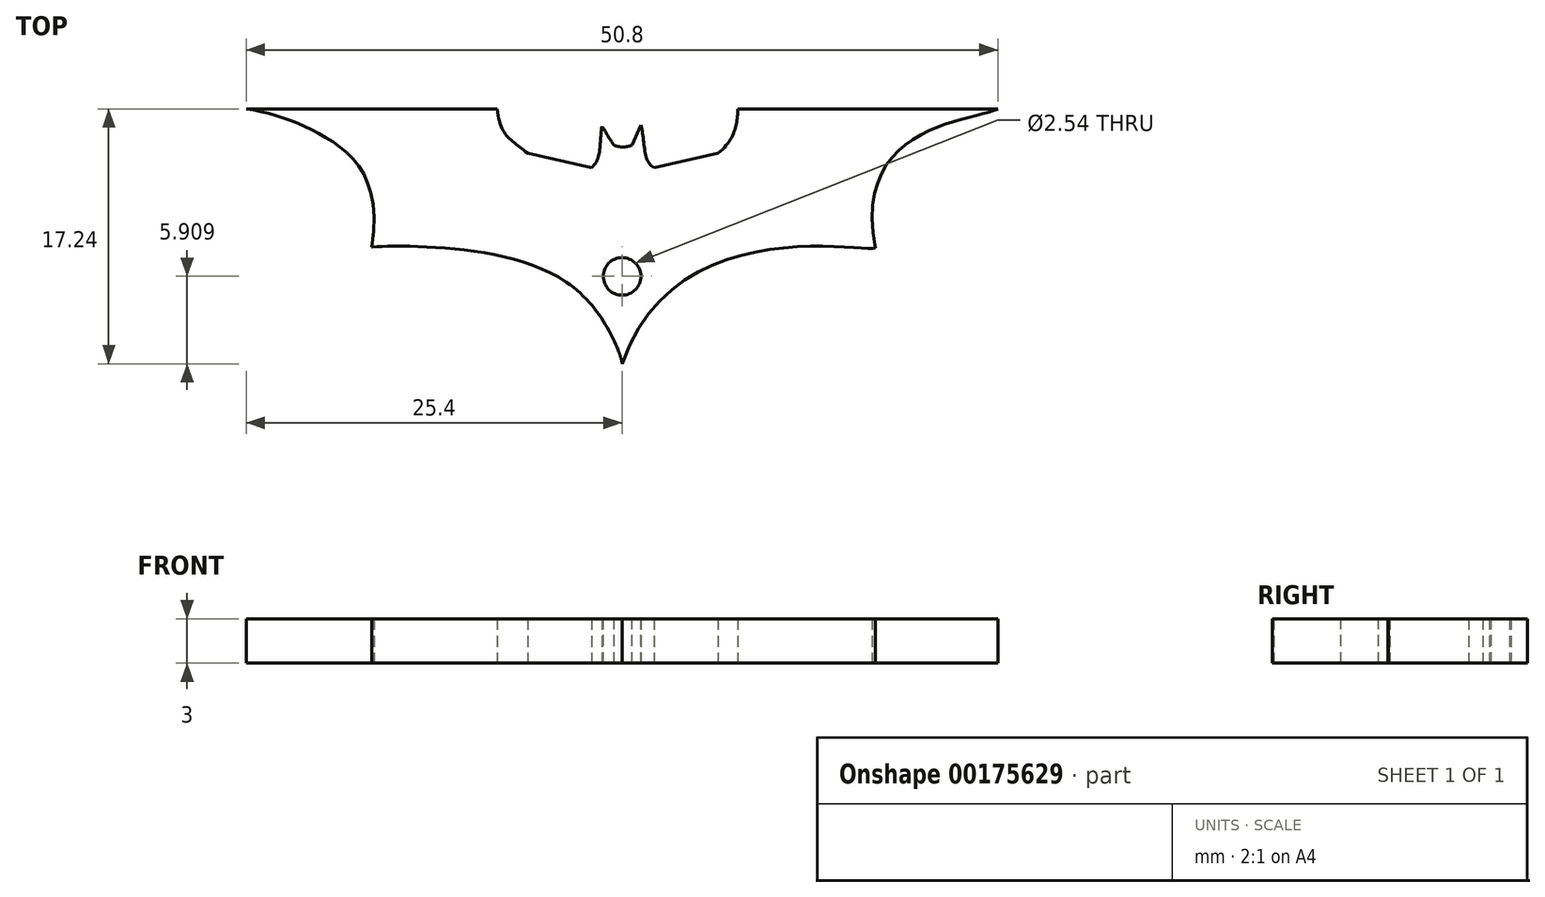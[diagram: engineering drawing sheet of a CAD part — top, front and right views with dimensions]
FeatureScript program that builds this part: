
annotation { "Feature Type Name" : "Feature", "Feature Type Description" : "" }
export const myFeature = defineFeature(function(context is Context, id is Id, definition is map)
    precondition{}
    {
        {
            var Q0;
            Q0=qCreatedBy(makeId("Top.planeOp"),FACE);
            var sketch = newSketch(context, id + "F0", { "sketchPlane" : qUnion([Q0])});
            skLineSegment(sketch, "E0", {"start": v(-25.4, 7.55) * mm, "end": v(-8.43, 7.55) * mm});
            skLineSegment(sketch, "E1", {"start": v(7.83, 7.55) * mm, "end": v(25.4, 7.55) * mm});
            skLineSegment(sketch, "E2", {"start": v(-6.39, 4.53) * mm, "end": v(-2.06, 3.58) * mm});
            skLineSegment(sketch, "E3", {"start": v(2.17, 3.58) * mm, "end": v(6.5, 4.53) * mm});
            skFitSpline(sketch, "E4", {"points": [v(-25.4, 7.55) * mm, v(-20.42, 5.83) * mm, v(-16.9, -1.79) * mm], "startDerivative": vector(11.89, -1.77) * mm, "endDerivative": vector(-4.02, -25.55) * mm});
            skFitSpline(sketch, "E5", {"points": [v(-16.9, -1.79) * mm, v(-3.77, -4.17) * mm, v(0, -9.61) * mm, v(0, -9.71) * mm], "startDerivative": vector(11.09, 0.53) * mm, "endDerivative": vector(-0.62, -1.23) * mm});
            skFitSpline(sketch, "E6", {"points": [v(0.01, -9.7) * mm, v(17.12, -1.86) * mm], "startDerivative": vector(10.4, 30.75) * mm, "endDerivative": vector(3.02, 0.9) * mm});
            skFitSpline(sketch, "E7", {"points": [v(17.12, -1.86) * mm, v(25.4, 7.55) * mm], "startDerivative": vector(-4.83, 25.07) * mm, "endDerivative": vector(5.9, 2.68) * mm});
            skFitSpline(sketch, "E8", {"points": [v(6.5, 4.53) * mm, v(7.83, 7.55) * mm], "startDerivative": vector(3.62, 3.17) * mm, "endDerivative": vector(0.15, 2.98) * mm});
            skFitSpline(sketch, "E9", {"points": [v(-6.39, 4.53) * mm, v(-8.43, 7.55) * mm], "startDerivative": vector(-3.17, 2.72) * mm, "endDerivative": vector(-0.45, 5.55) * mm});
            skFitSpline(sketch, "E10", {"points": [v(-2.06, 3.58) * mm, v(-1.35, 6.35) * mm], "startDerivative": vector(2.27, 1.81) * mm, "endDerivative": vector(0.6, 2.67) * mm});
            skFitSpline(sketch, "E11", {"points": [v(-1.35, 6.35) * mm, v(-0.55, 5.09) * mm], "startDerivative": vector(0.9, -1.16) * mm, "endDerivative": vector(0.9, -1.16) * mm});
            skFitSpline(sketch, "E12", {"points": [v(1.26, 6.45) * mm, v(2.17, 3.58) * mm], "startDerivative": vector(0.9, -2.9) * mm, "endDerivative": vector(2.42, -0.9) * mm});
            skFitSpline(sketch, "E13", {"points": [v(-0.55, 5.09) * mm, v(0.66, 5.09) * mm], "startDerivative": vector(1.15, -0.5) * mm, "endDerivative": vector(1.1, 0.5) * mm});
            skLineSegment(sketch, "E14", {"start": v(1.26, 6.45) * mm, "end": v(0.66, 5.09) * mm});
            skFitSpline(sketch, "E15", {"points": [v(-25.4, 7.55) * mm, v(-20.42, 5.83) * mm, v(-16.9, -1.79) * mm], "startDerivative": vector(11.89, -1.77) * mm, "endDerivative": vector(-4.02, -25.55) * mm});
            skFitSpline(sketch, "E16", {"points": [v(-16.9, -1.79) * mm, v(-3.77, -4.17) * mm, v(0.01, -9.7) * mm], "startDerivative": vector(10.58, 0.5) * mm, "endDerivative": vector(0.07, -2.6) * mm});
            skLineSegment(sketch, "E17", {"start": v(-25.4, 7.55) * mm, "end": v(25.4, 7.55) * mm});
            skPoint(sketch, "E18", {"position": v(0, 7.55) * mm});
            skSolve(sketch);
        }
        {
            var Q0;
            {var subQ0=sQuery(id+"F0.wireOp",EDGE,"E16");var subQ1=sQuery(id+"F0.wireOp",EDGE,"E5");var subQ3=makeQuery(id+"F0.imprint","INTERSECT",VERTEX,{"disambiguationData":[OD(1.0)],"derivedFrom":[subQ1,subQ0]});Q0=makeQuery(id+"F0.imprint","IMPRINT",FACE,{"disambiguationData":[TD([[makeQuery(id+"F0.imprint","IMPRINT",EDGE,{"disambiguationData":[TD([[subQ3,1.0]])],"derivedFrom":subQ1}),1.0]])]});}
            var Q1;
            {var subQ0=sQuery(id+"F0.wireOp",EDGE,"E16");var subQ1=sQuery(id+"F0.wireOp",EDGE,"E5");var subQ2=makeQuery(id+"F0.imprint","INTERSECT",VERTEX,{"disambiguationData":[OD(1.0)],"derivedFrom":[subQ1,subQ0]});Q1=makeQuery(id+"F0.imprint","IMPRINT",FACE,{"disambiguationData":[TD([[makeQuery(id+"F0.imprint","IMPRINT",EDGE,{"disambiguationData":[TD([[subQ2,-1.0]])],"derivedFrom":subQ1}),-1.0]])]});}
            var Q2;
            {var subQ0=sQuery(id+"F0.wireOp",EDGE,"E16");var subQ1=sQuery(id+"F0.wireOp",EDGE,"E5");var subQ2=makeQuery(id+"F0.imprint","INTERSECT",VERTEX,{"disambiguationData":[OD(2.0)],"derivedFrom":[subQ1,subQ0]});Q2=makeQuery(id+"F0.imprint","IMPRINT",FACE,{"disambiguationData":[TD([[makeQuery(id+"F0.imprint","IMPRINT",EDGE,{"disambiguationData":[TD([[subQ2,-1.0]])],"derivedFrom":subQ1}),1.0]])]});}
            var Q3;
            {var subQ0=sQuery(id+"F0.wireOp",EDGE,"E16");var subQ1=sQuery(id+"F0.wireOp",EDGE,"E5");var subQ2=makeQuery(id+"F0.imprint","INTERSECT",VERTEX,{"disambiguationData":[OD(0.0)],"derivedFrom":[subQ1,subQ0]});Q3=makeQuery(id+"F0.imprint","IMPRINT",FACE,{"disambiguationData":[TD([[makeQuery(id+"F0.imprint","IMPRINT",EDGE,{"disambiguationData":[TD([[subQ2,1.0]])],"derivedFrom":subQ1}),-1.0]])]});}
            var Q4;
            Q4=makeQuery(id+"F0.imprint","IMPRINT",FACE,{"disambiguationData":[TD([[makeQuery(id+"F0.imprint","IMPRINT",EDGE,{"derivedFrom":sQuery(id+"F0.wireOp",EDGE,"E2")}),-1.0]])]});
            extrude(context, id + "F1", {"entities" : qUnion([Q0, Q1, Q2, Q3, Q4]), "offsetDistance" : 25 * mm, "depth" : 3 * mm});
        }
        {
            var Q0;
            Q0=makeQuery(id+"F1.opExtrude","CAP_FACE",FACE,{"disambiguationData":[OSD([sQuery(id+"F0.wireOp",EDGE,"E1"),sQuery(id+"F0.wireOp",EDGE,"E2"),sQuery(id+"F0.wireOp",EDGE,"E3"),sQuery(id+"F0.wireOp",EDGE,"E5"),sQuery(id+"F0.wireOp",EDGE,"E6"),sQuery(id+"F0.wireOp",EDGE,"E7"),sQuery(id+"F0.wireOp",EDGE,"E8"),sQuery(id+"F0.wireOp",EDGE,"E9"),sQuery(id+"F0.wireOp",EDGE,"E10"),sQuery(id+"F0.wireOp",EDGE,"E11"),sQuery(id+"F0.wireOp",EDGE,"E12"),sQuery(id+"F0.wireOp",EDGE,"E13"),sQuery(id+"F0.wireOp",EDGE,"E14"),sQuery(id+"F0.wireOp",EDGE,"E0"),sQuery(id+"F0.wireOp",EDGE,"E15"),sQuery(id+"F0.wireOp",EDGE,"E16")])],"isStart":false});
            var sketch = newSketch(context, id + "F2", { "sketchPlane" : qUnion([Q0])});
            skCircle(sketch, "E19", {"center": v(0, -3.78) * mm, "radius": 1.27 * mm});
            skSolve(sketch);
        }
        {
            var Q0;
            Q0=makeQuery(id+"F2.imprint","IMPRINT",FACE,{"disambiguationData":[TD([[makeQuery(id+"F2.imprint","IMPRINT",EDGE,{"derivedFrom":sQuery(id+"F2.wireOp",EDGE,"E19")}),1.0]])]});
            extrude(context, id + "F3", {"entities" : qUnion([Q0]), "operationType" : NewBodyOperationType.REMOVE, "oppositeDirection" : true, "offsetDistance" : 25 * mm, "depth" : 3 * mm});
        }
    });
